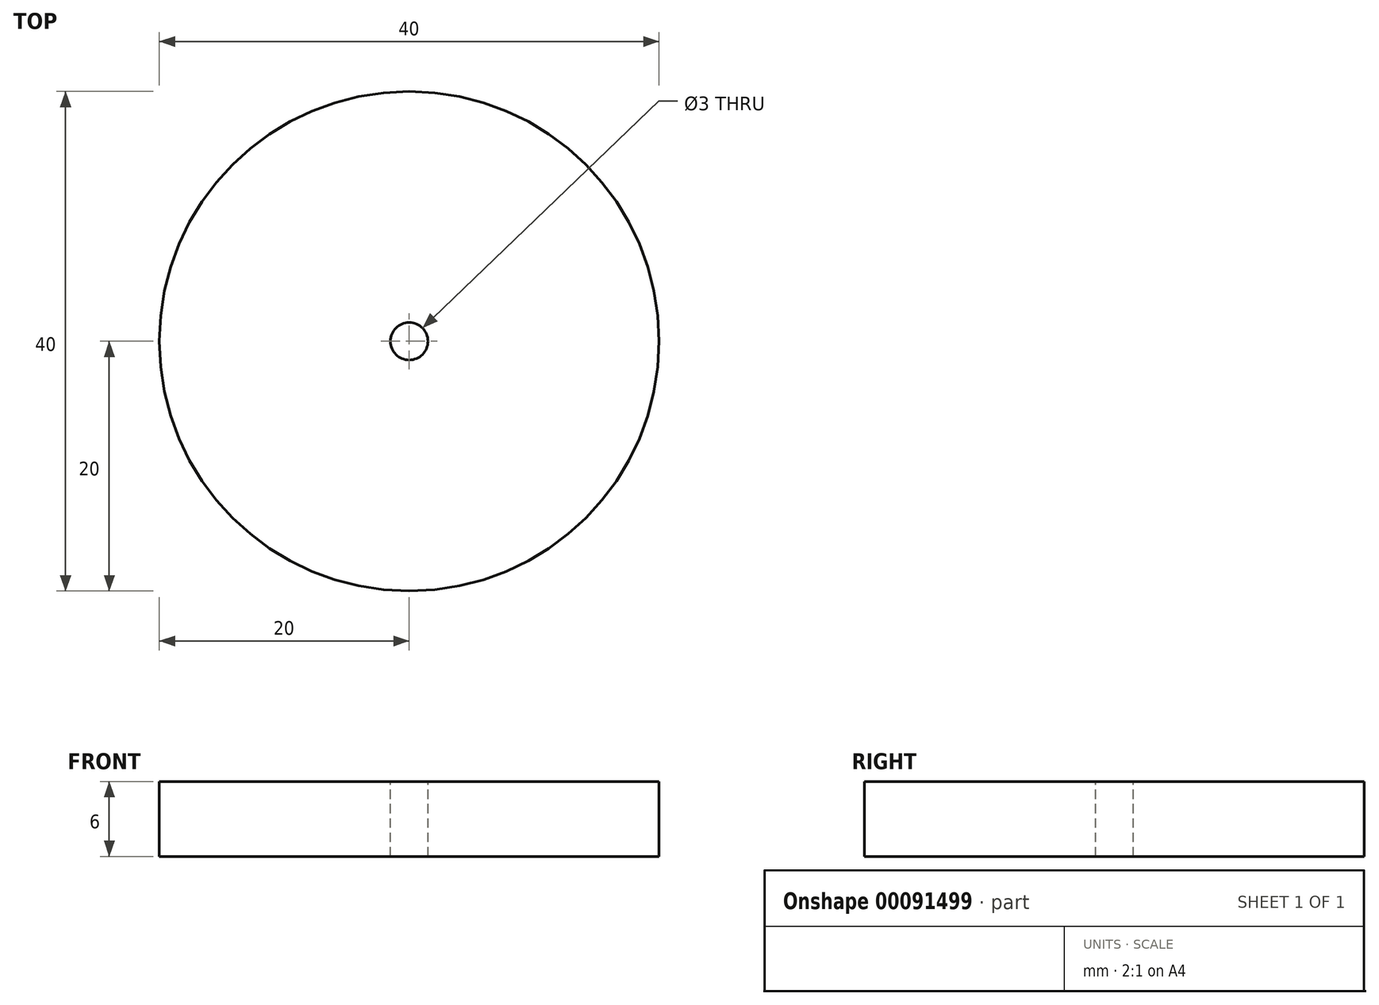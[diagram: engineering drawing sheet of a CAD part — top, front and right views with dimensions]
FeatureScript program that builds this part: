
annotation { "Feature Type Name" : "Feature", "Feature Type Description" : "" }
export const myFeature = defineFeature(function(context is Context, id is Id, definition is map)
    precondition{}
    {
        {
            var Q0;
            Q0=qCreatedBy(makeId("Top.planeOp"),FACE);
            var sketch = newSketch(context, id + "F0", { "sketchPlane" : qUnion([Q0])});
            skCircle(sketch, "E0", {"center": v(0, 0) * mm, "radius": 20 * mm});
            skSolve(sketch);
        }
        {
            var Q0;
            Q0=makeQuery(id+"F0.imprint","IMPRINT",FACE,{"disambiguationData":[TD([[makeQuery(id+"F0.imprint","IMPRINT",EDGE,{"derivedFrom":sQuery(id+"F0.wireOp",EDGE,"E0")}),1.0]])]});
            var Q1;
            Q1=sQuery(id+"F0.wireOp",EDGE,"E0");
            extrude(context, id + "F1", {"entities" : qUnion([Q0]), "surfaceEntities" : qUnion([Q1]), "endBound" : BoundingType.SYMMETRIC, "depth" : 6 * mm});
        }
        {
            var Q0;
            Q0=sQuery(id+"F0.wireOp",VERTEX,"E0.center");
            var Q1;
            Q1=makeQuery(id+"F1.opExtrude","SWEPT_BODY",BODY,{"disambiguationData":[OSD([sQuery(id+"F0.wireOp",EDGE,"E0")])]});
            hole(context, id + "F2", {"style" : HoleStyle.SIMPLE, "endStyle" : HoleEndStyle.THROUGH, "holeDiameter" : 3 * mm, "locations" : qUnion([Q0]), "scope" : qUnion([Q1]), "isTappedThrough" : true});
        }
        {
            var Q0;
            Q0=sQuery(id+"F0.wireOp",VERTEX,"E0.center");
            var Q1;
            Q1=makeQuery(id+"F1.opExtrude","SWEPT_BODY",BODY,{"disambiguationData":[OSD([sQuery(id+"F0.wireOp",EDGE,"E0")])]});
            hole(context, id + "F3", {"style" : HoleStyle.SIMPLE, "endStyle" : HoleEndStyle.THROUGH, "oppositeDirection" : true, "holeDiameter" : 3 * mm, "locations" : qUnion([Q0]), "scope" : qUnion([Q1]), "isTappedThrough" : true});
        }
    });
